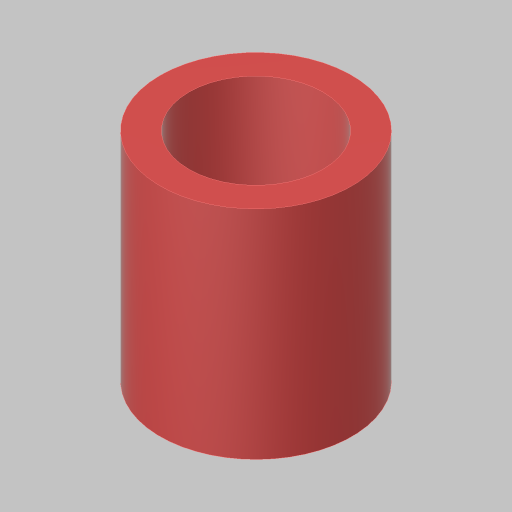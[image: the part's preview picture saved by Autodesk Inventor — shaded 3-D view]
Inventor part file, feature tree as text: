
AUTODESK INVENTOR PART (.ipt)
format: ipt  version: 2023.5 (Build 275446000, 446)  size: 104,960 bytes
history: native  units: in
note: dims shown in document units (in); Inventor stores cm internally (conversion verified against a paired STEP export)
features: extrude x1, sketch x1
ambient origin geometry x8: Origin, YZ Plane, XZ Plane, XY Plane, X Axis, Y Axis, Z Axis, Center Point
bodies: Solid1 (feature_tree)
feature tree (2):
  extrude  "Extrusion1"  Depth=0.94in
  sketch  "Sketch1"  dims[d0=0.58in d1=0.125in d2=0.94in d3=0.0in]
